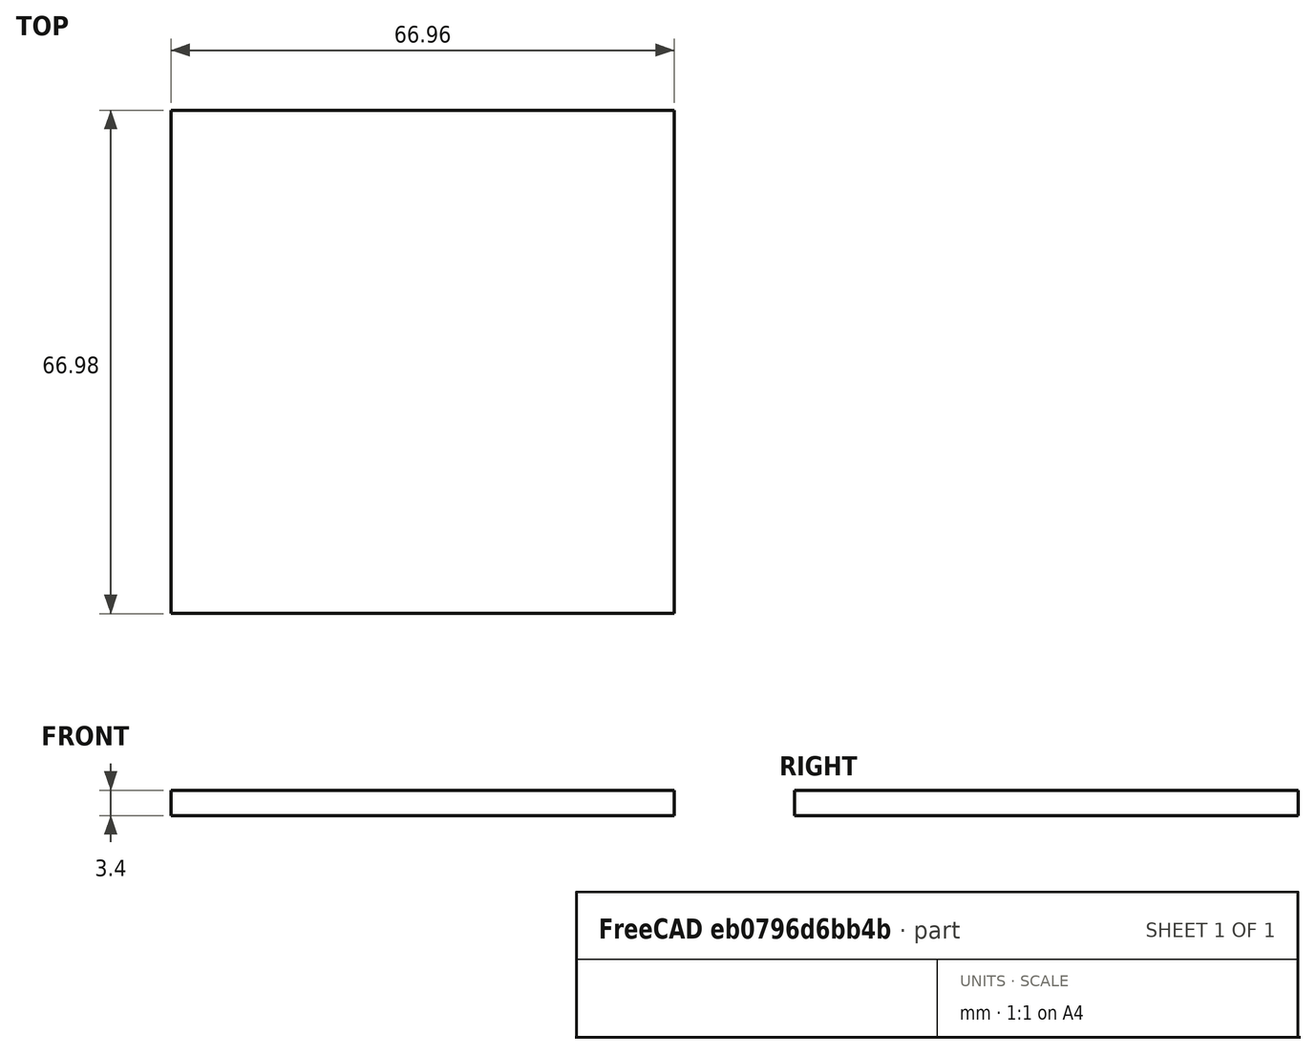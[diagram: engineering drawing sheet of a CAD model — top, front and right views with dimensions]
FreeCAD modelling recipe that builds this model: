
FCSTD DOCUMENT  (FreeCAD 0.17R12703 (Git))
Label: Heckspant
License: All rights reserved
LicenseURL: http://en.wikipedia.org/wiki/All_rights_reserved
objects: Path::FeaturePython×7, Part::FeaturePython×2, Part::Feature×1, App::FeaturePython×1, Path::FeatureCompoundPython×1
note: 5 computed .brp shape members not serialized (recipe doc carries the construction recipe); baked Part::Feature solids carry a one-line shape summary decoded from their .brp

FEATURE [Part::Feature] Part__Feature  label="Heckspant"
  Placement = pos=(0,0,-3.4) rot=(0,0,1;0rad)
  shape: bbox 66.96 x 67 x 3.4 mm, 17 faces (baked)
FEATURE [App::FeaturePython] SetupSheet  # Path/CAM operation (typed FeaturePython)
  ClearanceHeightExpression = StartDepth+SetupSheet.ClearanceHeightOffset
  ClearanceHeightOffset = 5
  FinalDepthExpression = OpFinalDepth
  HorizRapid = 0
  SafeHeightExpression = StartDepth+SetupSheet.SafeHeightOffset
  SafeHeightOffset = 3
  StartDepthExpression = OpStartDepth
  StepDownExpression = OpToolDiameter
  VertRapid = 0
FEATURE [Part::FeaturePython] Clone  label="Base-Heckspant"  # Draft clone (typed FeaturePython)
  AttacherType = Attacher::AttachEngine3D
  Fuse = false
  Objects = -> [Part__Feature]
  PathResource = Base
  Placement = pos=(0,0,-3.4) rot=(0,0,1;0rad)
  Scale = (1,1,1)
FEATURE [Path::FeaturePython] T1__Schaftfraeser_D2  label="T1: Schaftfraeser_D2"  # Path/CAM operation (typed FeaturePython)
  HorizFeed = 400
  HorizRapid = 0
  SpindleDir = 0
  SpindleSpeed = 0
  ToolNumber = 1
  VertFeed = 100
  VertRapid = 0
  expr: VertRapid = SetupSheet.VertRapid
  expr: HorizRapid = SetupSheet.HorizRapid
FEATURE [Part::FeaturePython] Stock  # WARN: FeaturePython — macro-defined, semantics opaque (R4)
  Base = -> Part__Feature
  ExtXneg = 0
  ExtXpos = 0
  ExtYneg = 0
  ExtYpos = 0
  ExtZneg = 0
  ExtZpos = 0
  StockType = FromBase
FEATURE [Path::FeaturePython] Profile_Edges  # Path/CAM operation (typed FeaturePython)
  Active = true
  AreaParams:
    OpenMode = 0
    Angle = 45.0
    MinArcPoints = 4
    Coplanar = 0
    Tolerance = 1e-07
    CleanDistance = 0.0
    PocketExtraOffset = 0.0
    AngleShift = 0.0
    SubjectFill = 0
    RoundPreceision = 0.0
    Simplify = False
    SectionTolerance = 1e-06
    MaxArcPoints = 100
    SectionOffset = 0.0
    Offset = -1.0
    Accuracy = 0.01
    PocketStepover = 0.0
    ClipFill = 0
    ToolRadius = 1.0
    Outline = False
    ClipperScale = 10000000.0
    FromCenter = False
    Explode = False
    EndType = 0
    Shift = 0.0
    ExtraPass = 0
    Project = False
    JoinType = 0
    Thicken = False
    Stepdown = 1.0
    SectionMode = 2
    MiterLimit = 2.0
    Deflection = 0.01
    Reorient = True
    FitArcs = True
    SectionCount = -1
    PocketMode = 0
    Stepover = 0.0
    Unit = 1.0
    Fill = 0
  Base = -> [Clone]
  ClearanceHeight = 5
  Direction = 0
  FinalDepth = -3.7
  JoinType = 0
  MiterLimit = 0.1
  OffsetExtra = 0
  OpFinalDepth = -3.4
  OpStartDepth = 0
  OpToolDiameter = 2
  PathParams = {'resume_height': 3.0, 'feedrate': 400.0, 'verbose': True, 'orientation': 1, 'return_end': True, 'preamble': False, 'retraction': 5.0, 'feedrate_v': 100.0}
  SafeHeight = 3
  Side = 1
  StartDepth = 0
  StartPoint = (0,0,0)
  StepDown = 2
  ToolController = -> T1__Schaftfraeser_D2
  UseComp = true
  UseStartPoint = false
  expr: ClearanceHeight = StartDepth + SetupSheet.ClearanceHeightOffset
  expr: SafeHeight = StartDepth + SetupSheet.SafeHeightOffset
  expr: StepDown = 2
  expr: FinalDepth = -3.7000000000000002
  expr: StartDepth = OpStartDepth
FEATURE [Path::FeaturePython] TagDressup  # Path/CAM operation (typed FeaturePython)
  Angle = 45
  Base = -> Profile_Edges
  Height = 1.6
  Positions = (2) [(24.2038,10.7891,0),(-24.4444,-10.2256,0)]
  Radius = 0
  SegmentationFactor = 50
  Width = 4
FEATURE [Path::FeaturePython] Contour  # Path/CAM operation (typed FeaturePython)
  Active = true
  AreaParams:
    OpenMode = 0
    Angle = 45.0
    MinArcPoints = 4
    Coplanar = 2
    Tolerance = 1e-07
    CleanDistance = 0.0
    PocketExtraOffset = 0.0
    AngleShift = 0.0
    SubjectFill = 0
    RoundPreceision = 0.0
    Simplify = False
    SectionTolerance = 1e-06
    MaxArcPoints = 100
    SectionOffset = 0.0
    Offset = 1.0
    Accuracy = 0.01
    PocketStepover = 0.0
    ClipFill = 0
    ToolRadius = 1.0
    Outline = False
    ClipperScale = 10000000.0
    FromCenter = False
    Explode = False
    EndType = 0
    Shift = 0.0
    ExtraPass = 0
    Project = False
    JoinType = 0
    Thicken = False
    Stepdown = 1.0
    SectionMode = 2
    MiterLimit = 2.0
    Deflection = 0.01
    Reorient = True
    FitArcs = True
    SectionCount = -1
    PocketMode = 0
    Stepover = 0.0
    Unit = 1.0
    Fill = 0
  ClearanceHeight = 5
  Direction = 1
  FinalDepth = -3.7
  JoinType = 0
  MiterLimit = 0.1
  OffsetExtra = 0
  OpFinalDepth = -3.4
  OpStartDepth = 0
  OpToolDiameter = 2
  PathParams = {'resume_height': 3.0, 'feedrate': 400.0, 'verbose': True, 'orientation': 0, 'return_end': True, 'preamble': False, 'retraction': 5.0, 'feedrate_v': 100.0}
  SafeHeight = 3
  Side = 0
  StartDepth = 0
  StartPoint = (0,0,0)
  StepDown = 2
  ToolController = -> T1__Schaftfraeser_D2
  UseComp = true
  UseStartPoint = false
  expr: ClearanceHeight = StartDepth + SetupSheet.ClearanceHeightOffset
  expr: SafeHeight = StartDepth + SetupSheet.SafeHeightOffset
  expr: StepDown = 2
  expr: FinalDepth = -3.7000000000000002
  expr: StartDepth = OpStartDepth
FEATURE [Path::FeaturePython] DogboneDressup  # Path/CAM operation (typed FeaturePython)
  Base = -> Contour
  Custom = 0
  Incision = 0
  Side = 0
  Style = 0
  ToolController = -> T1__Schaftfraeser_D2
FEATURE [Path::FeaturePython] TagDressup001  # Path/CAM operation (typed FeaturePython)
  Angle = 45
  Base = -> DogboneDressup
  Height = 1.6
  Positions = (3) [(-17.2499,29.8776,0),(-23.3041,-25.4392,0),(34.3091,-3.62143,0)]
  Radius = 0
  SegmentationFactor = 50
  Width = 4
FEATURE [Path::FeatureCompoundPython] Operations  # Path/CAM operation (typed FeaturePython)
  Group = -> [TagDressup,TagDressup001]
  UsePlacements = false
FEATURE [Path::FeaturePython] Job  # Path/CAM operation (typed FeaturePython)
  Base = -> Clone
  GeometryTolerance = 0.01
  Operations = -> Operations
  PostProcessor = 5
  SetupSheet = -> SetupSheet
  Stock = -> Stock
  ToolController = -> [T1__Schaftfraeser_D2]
